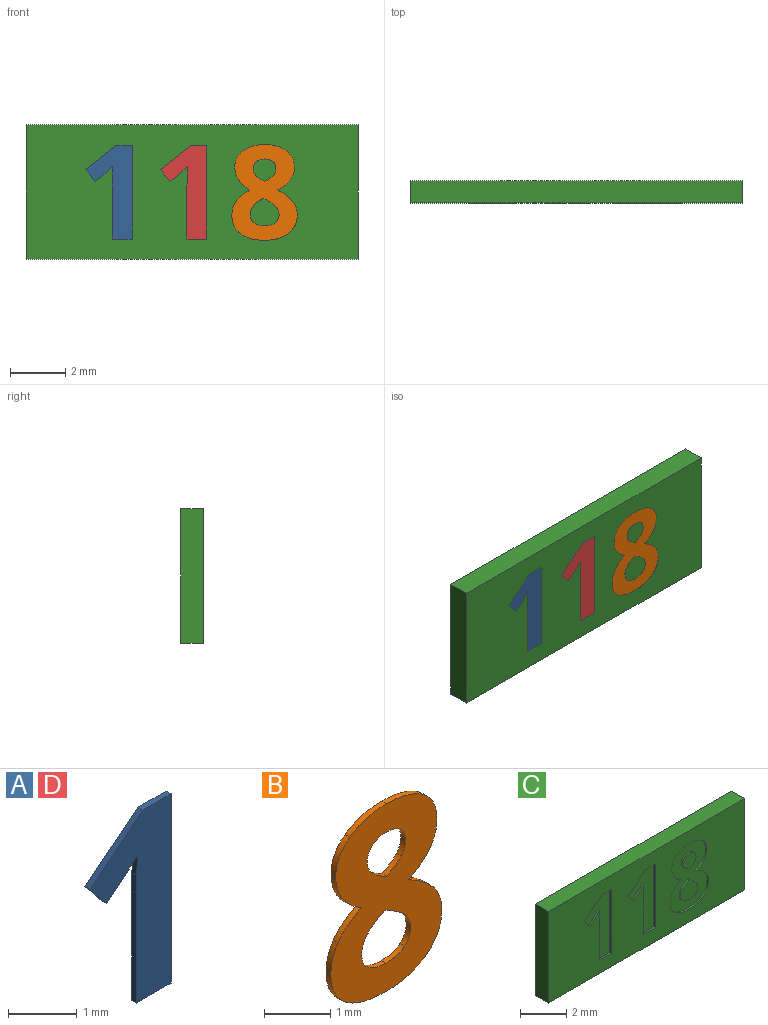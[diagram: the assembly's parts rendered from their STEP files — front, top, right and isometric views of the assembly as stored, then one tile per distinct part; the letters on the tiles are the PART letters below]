
ASSEMBLY  parts=4 mates=4
PART A: 12 faces, bbox 1.7x0.1x3.4 mm
  f0: plane 3.37x1.67mm, normal (0,-1,0), area 2.9mm2, adj f1,f2,f3,f4,f5,f6,f7,f9
  f1: plane 0.59x0.1mm, normal (0,0,1), area 0.1mm2, adj f0,f2,f8,f10
  f2: plane 1.09x0.86mm, normal (-0.62,0,0.78), area 0.1mm2, adj f0,f1,f3,f8
  f3: plane 0.43x0.34mm, normal (-0.78,0,-0.63), area 0.1mm2, adj f0,f2,f4,f8
  f4: plane 0.39x0.31mm, normal (0.63,0,-0.78), area 0mm2, adj f0,f3,f5,f8
  f5: extruded ~0.25x0.23mm, area 0mm2, adj f0,f4,f6,f8
  f6: plane 0.35x0.1mm, normal (-1,0,0.03), area 0mm2, adj f0,f5,f7,f8
  f7: plane 0.32x0.1mm, normal (-1,0,0.02), area 0mm2, adj f0,f6,f8,f9
  f8: plane 3.37x1.67mm, normal (0,1,0), area 2.9mm2, adj f1,f2,f3,f4,f5,f6,f7,f9
  f9: plane 1.95x0.1mm, normal (-1,0,0), area 0.2mm2, adj f0,f7,f8,f11
  f10: plane 3.37x0.1mm, normal (1,0,0), area 0.3mm2, adj f0,f1,f8,f11
  f11: plane 0.71x0.1mm, normal (0,0,-1), area 0.1mm2, adj f0,f8,f9,f10
PART B: 33 faces, bbox 2.4x0.1x3.5 mm
  f0: plane 3.46x2.37mm, normal (0,-1,0), area 5.2mm2, adj f1,f2,f3,f4,f5,f6,f7,f8
  f1: extruded ~0.59x0.3mm, area 0.1mm2, adj f0,f2,f23,f25
  f2: extruded ~0.45x0.13mm, area 0mm2, adj f0,f1,f3,f23
  f3: extruded ~0.42x0.39mm, area 0.1mm2, adj f0,f2,f4,f23
  f4: extruded ~0.49x0.39mm, area 0.1mm2, adj f0,f3,f5,f23
  f5: extruded ~0.51x0.15mm, area 0.1mm2, adj f0,f4,f6,f23
  f6: extruded ~0.67x0.32mm, area 0.1mm2, adj f0,f5,f7,f23
  f7: extruded ~0.87x0.24mm, area 0.1mm2, adj f0,f6,f8,f23
  f8: extruded ~0.86x0.25mm, area 0.1mm2, adj f0,f7,f9,f23
  f9: extruded ~0.67x0.33mm, area 0.1mm2, adj f0,f8,f10,f23
  f10: extruded ~0.48x0.17mm, area 0.1mm2, adj f0,f9,f11,f23
  f11: extruded ~0.54x0.42mm, area 0.1mm2, adj f0,f10,f12,f23
  f12: extruded ~0.46x0.36mm, area 0.1mm2, adj f0,f11,f13,f23
  f13: extruded ~0.46x0.14mm, area 0mm2, adj f0,f12,f23,f24
  f14: extruded ~0.42x0.29mm, area 0.1mm2, adj f0,f15,f23,f31
  f15: extruded ~0.29x0.13mm, area 0mm2, adj f0,f14,f16,f23
  f16: extruded ~0.3x0.13mm, area 0mm2, adj f0,f15,f17,f23
  f17: extruded ~0.4x0.11mm, area 0mm2, adj f0,f16,f23,f30
  f18: extruded ~0.25x0.12mm, area 0mm2, adj f0,f19,f23,f28
  f19: extruded ~0.26x0.1mm, area 0mm2, adj f0,f18,f20,f23
  f20: extruded ~0.32x0.22mm, area 0mm2, adj f0,f19,f21,f23
  f21: extruded ~0.32x0.22mm, area 0mm2, adj f0,f20,f22,f23
  f22: extruded ~0.25x0.1mm, area 0mm2, adj f0,f21,f23,f27
  f23: plane 3.46x2.37mm, normal (0,1,0), area 5.2mm2, adj f1,f2,f3,f4,f5,f6,f7,f8
  f24: extruded ~0.59x0.3mm, area 0.1mm2, adj f0,f13,f23,f26
  f25: extruded ~0.78x0.22mm, area 0.1mm2, adj f0,f1,f23,f26
  f26: extruded ~0.78x0.22mm, area 0.1mm2, adj f0,f23,f24,f25
  f27: extruded ~0.25x0.11mm, area 0mm2, adj f0,f22,f23,f29
  f28: extruded ~0.3x0.1mm, area 0mm2, adj f0,f18,f23,f29
  f29: extruded ~0.29x0.1mm, area 0mm2, adj f0,f23,f27,f28
  f30: extruded ~0.38x0.11mm, area 0mm2, adj f0,f17,f23,f32
  f31: extruded ~0.57x0.49mm, area 0.1mm2, adj f0,f14,f23,f32
  f32: extruded ~0.31x0.14mm, area 0mm2, adj f0,f23,f30,f31
PART C: 62 faces, bbox 12x0.8x4.9 mm
  f0: plane 12x4.85mm, normal (0,-1,0), area 45.8mm2, adj f1,f2,f3,f4,f6,f7,f8,f9
  f1: plane 12x0.8mm, normal (0,0,-1), area 9.6mm2, adj f0,f2,f4,f5
  f2: plane 4.85x0.8mm, normal (1,0,0), area 3.9mm2, adj f0,f1,f3,f5
  f3: plane 12x0.8mm, normal (0,0,1), area 9.6mm2, adj f0,f2,f4,f5
  f4: plane 4.85x0.8mm, normal (-1,0,0), area 3.9mm2, adj f0,f1,f3,f5
  f5: plane 12x4.85mm, normal (0,1,0), area 58.2mm2, adj f1,f2,f3,f4
  f6: extruded ~0.78x0.22mm, area 0.1mm2, adj f0,f7,f36,f37
  f7: extruded ~0.59x0.3mm, area 0.1mm2, adj f0,f6,f8,f37
  f8: extruded ~0.45x0.13mm, area 0mm2, adj f0,f7,f9,f37
  f9: extruded ~0.42x0.39mm, area 0.1mm2, adj f0,f8,f10,f37
  f10: extruded ~0.49x0.39mm, area 0.1mm2, adj f0,f9,f11,f37
  f11: extruded ~0.51x0.15mm, area 0.1mm2, adj f0,f10,f12,f37
  f12: extruded ~0.67x0.32mm, area 0.1mm2, adj f0,f11,f13,f37
  f13: extruded ~0.87x0.24mm, area 0.1mm2, adj f0,f12,f14,f37
  f14: extruded ~0.86x0.25mm, area 0.1mm2, adj f0,f13,f15,f37
  f15: extruded ~0.67x0.33mm, area 0.1mm2, adj f0,f14,f16,f37
  f16: extruded ~0.48x0.17mm, area 0.1mm2, adj f0,f15,f17,f37
  f17: extruded ~0.54x0.42mm, area 0.1mm2, adj f0,f16,f18,f37
  f18: extruded ~0.46x0.36mm, area 0.1mm2, adj f0,f17,f19,f37
  f19: extruded ~0.46x0.14mm, area 0mm2, adj f0,f18,f20,f37
  f20: extruded ~0.59x0.3mm, area 0.1mm2, adj f0,f19,f36,f37
  f21: extruded ~0.57x0.49mm, area 0.1mm2, adj f22,f34,f37,f39
  f22: extruded ~0.42x0.29mm, area 0.1mm2, adj f21,f23,f37,f39
  f23: extruded ~0.29x0.13mm, area 0mm2, adj f22,f24,f37,f39
  f24: extruded ~0.3x0.13mm, area 0mm2, adj f23,f25,f37,f39
  f25: extruded ~0.4x0.11mm, area 0mm2, adj f24,f26,f37,f39
  f26: extruded ~0.38x0.11mm, area 0mm2, adj f25,f34,f37,f39
  f27: extruded ~0.3x0.1mm, area 0mm2, adj f28,f35,f37,f38
  f28: extruded ~0.25x0.12mm, area 0mm2, adj f27,f29,f37,f38
  f29: extruded ~0.26x0.1mm, area 0mm2, adj f28,f30,f37,f38
  f30: extruded ~0.32x0.22mm, area 0mm2, adj f29,f31,f37,f38
  f31: extruded ~0.32x0.22mm, area 0mm2, adj f30,f32,f37,f38
  f32: extruded ~0.25x0.1mm, area 0mm2, adj f31,f33,f37,f38
  f33: extruded ~0.25x0.11mm, area 0mm2, adj f32,f35,f37,f38
  f34: extruded ~0.31x0.14mm, area 0mm2, adj f21,f26,f37,f39
  f35: extruded ~0.29x0.1mm, area 0mm2, adj f27,f33,f37,f38
  f36: extruded ~0.78x0.22mm, area 0.1mm2, adj f0,f6,f20,f37
  f37: plane 3.46x2.37mm, normal (0,-1,0), area 5.2mm2, adj f6,f7,f8,f9,f10,f11,f12,f13
  f38: plane 0.82x0.82mm, normal (0,-1,0), area 0.5mm2, adj f27,f28,f29,f30,f31,f32,f33,f35
  f39: plane 1.04x0.99mm, normal (0,-1,0), area 0.8mm2, adj f21,f22,f23,f24,f25,f26,f34
  f40: plane 3.37x0.1mm, normal (-1,0,0), area 0.3mm2, adj f0,f41,f49,f50
  f41: plane 0.59x0.1mm, normal (0,0,-1), area 0.1mm2, adj f0,f40,f42,f50
  f42: plane 1.09x0.86mm, normal (0.62,0,-0.78), area 0.1mm2, adj f0,f41,f43,f50
  f43: plane 0.43x0.34mm, normal (0.78,0,0.63), area 0.1mm2, adj f0,f42,f44,f50
  f44: plane 0.39x0.31mm, normal (-0.63,0,0.78), area 0mm2, adj f0,f43,f45,f50
  f45: extruded ~0.25x0.23mm, area 0mm2, adj f0,f44,f46,f50
  f46: plane 0.35x0.1mm, normal (1,0,-0.03), area 0mm2, adj f0,f45,f47,f50
  f47: plane 0.32x0.1mm, normal (1,0,-0.02), area 0mm2, adj f0,f46,f48,f50
  f48: plane 1.95x0.1mm, normal (1,0,0), area 0.2mm2, adj f0,f47,f49,f50
  f49: plane 0.71x0.1mm, normal (0,0,1), area 0.1mm2, adj f0,f40,f48,f50
  f50: plane 3.37x1.67mm, normal (0,-1,0), area 2.9mm2, adj f40,f41,f42,f43,f44,f45,f46,f47
  f51: plane 3.37x0.1mm, normal (-1,0,0), area 0.3mm2, adj f0,f52,f60,f61
  f52: plane 0.59x0.1mm, normal (0,0,-1), area 0.1mm2, adj f0,f51,f53,f61
  f53: plane 1.09x0.86mm, normal (0.62,0,-0.78), area 0.1mm2, adj f0,f52,f54,f61
  f54: plane 0.43x0.34mm, normal (0.78,0,0.63), area 0.1mm2, adj f0,f53,f55,f61
  f55: plane 0.39x0.31mm, normal (-0.63,0,0.78), area 0mm2, adj f0,f54,f56,f61
  f56: extruded ~0.25x0.23mm, area 0mm2, adj f0,f55,f57,f61
  f57: plane 0.35x0.1mm, normal (1,0,-0.03), area 0mm2, adj f0,f56,f58,f61
  f58: plane 0.32x0.1mm, normal (1,0,-0.02), area 0mm2, adj f0,f57,f59,f61
  f59: plane 1.95x0.1mm, normal (1,0,0), area 0.2mm2, adj f0,f58,f60,f61
  f60: plane 0.71x0.1mm, normal (0,0,1), area 0.1mm2, adj f0,f51,f59,f61
  f61: plane 3.37x1.67mm, normal (0,-1,0), area 2.9mm2, adj f51,f52,f53,f54,f55,f56,f57,f58
PART D: same geometry as A
PLACE A t=(-4.62,0.33,-0.04)mm
PLACE B t=(1.06,0.33,-0.04)mm
PLACE C t=(-0.07,0.33,-0.04)mm
PLACE D t=(-1.92,0.33,-0.04)mm
MATE fastened A.f0 <-> C.f0  axis (0,-1,0) through (-2.94,-0.47,-1.74)mm
MATE fastened A.f0 <-> C.f0  axis (0,-1,0) through (-2.94,-0.47,-1.74)mm
MATE fastened D.f0 <-> C.f0  axis (0,-1,0) through (-0.25,-0.47,-1.74)mm
MATE fastened B.f0 <-> C.f0  axis (0,-1,0) through (2.56,-0.47,-1.79)mm
